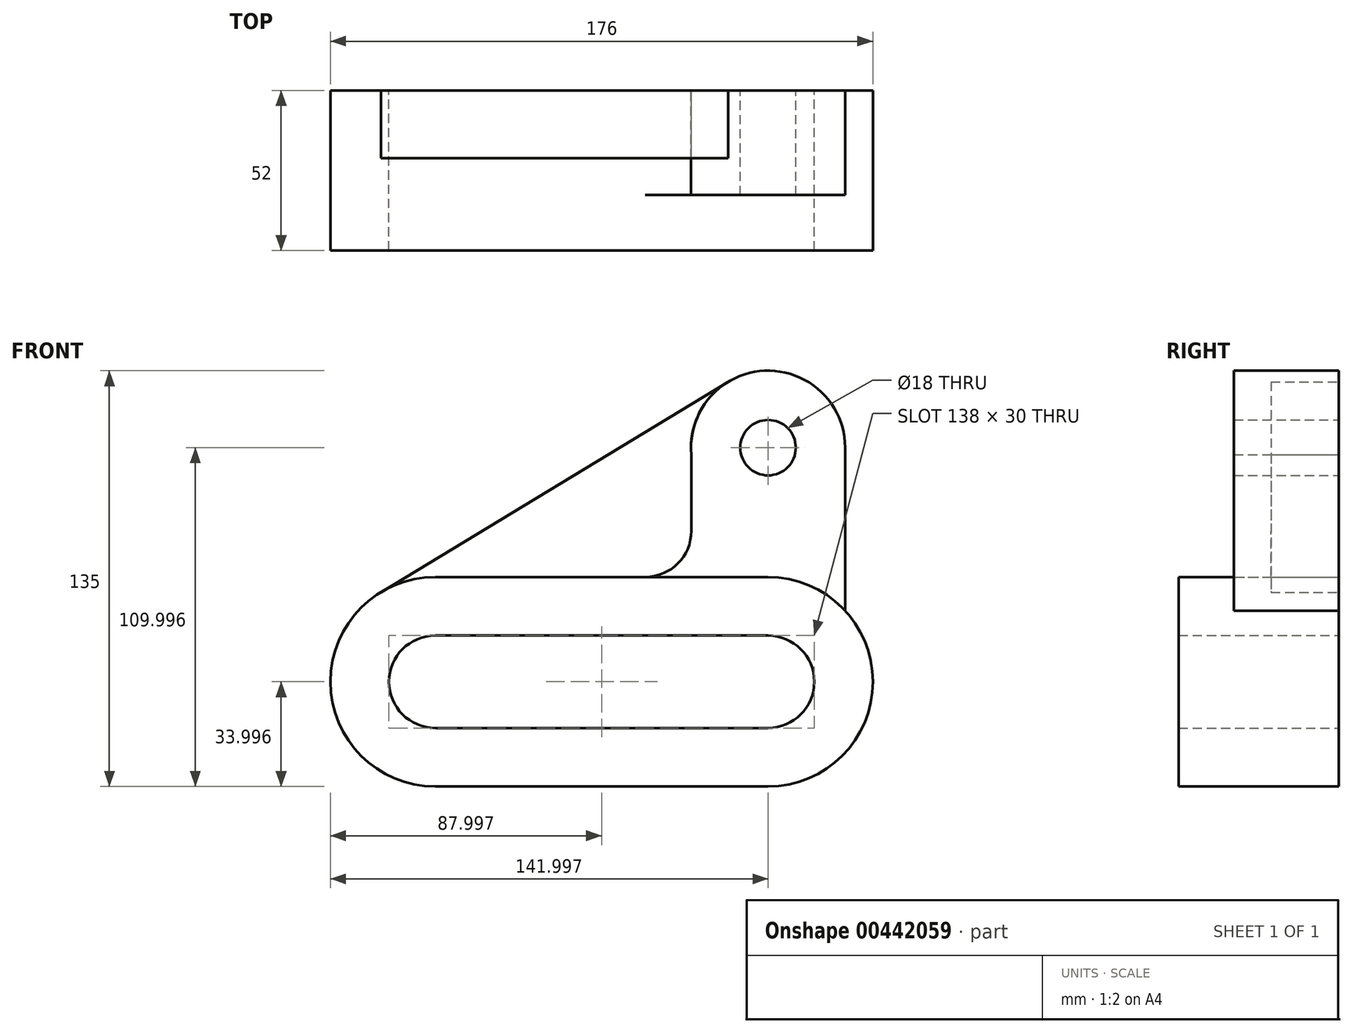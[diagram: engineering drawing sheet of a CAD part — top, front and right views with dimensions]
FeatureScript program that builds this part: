
annotation { "Feature Type Name" : "Feature", "Feature Type Description" : "" }
export const myFeature = defineFeature(function(context is Context, id is Id, definition is map)
    precondition{}
    {
        {
            var Q0;
            Q0=qCreatedBy(makeId("Front.planeOp"),FACE);
            var sketch = newSketch(context, id + "F0", { "sketchPlane" : qUnion([Q0])});
            skCircle(sketch, "E0", {"center": v(33.69, 22.6) * mm, "radius": 9 * mm});
            skCircle(sketch, "E1", {"center": v(33.69, 22.6) * mm, "radius": 25 * mm});
            skLineSegment(sketch, "E2.bottom", {"start": v(-74.31, -19.4) * mm, "end": v(-6.21, -19.4) * mm});
            skLineSegment(sketch, "E2.top", {"start": v(-74.31, -87.4) * mm, "end": v(33.69, -87.4) * mm});
            skLineSegment(sketch, "E2.left", {"start": v(-74.31, -19.4) * mm, "end": v(-74.31, -87.4) * mm});
            skLineSegment(sketch, "E2.right", {"start": v(33.69, -19.4) * mm, "end": v(33.69, -87.4) * mm});
            skCircle(sketch, "E3", {"center": v(-74.31, -53.4) * mm, "radius": 34 * mm});
            skCircle(sketch, "E4", {"center": v(33.69, -53.4) * mm, "radius": 34 * mm});
            skArc(sketch, "E5", {"start": v(-74.31, -38.4) * mm, "mid": v(-89.31, -53.4) * mm, "end": v(-74.31, -68.4) * mm});
            skArc(sketch, "E6", {"start": v(33.69, -68.4) * mm, "mid": v(48.69, -53.4) * mm, "end": v(33.69, -38.4) * mm});
            skLineSegment(sketch, "E7", {"start": v(-74.31, -38.4) * mm, "end": v(33.69, -38.4) * mm});
            skLineSegment(sketch, "E8", {"start": v(-74.31, -68.4) * mm, "end": v(33.69, -68.4) * mm});
            skLineSegment(sketch, "E9", {"start": v(20.73, 43.98) * mm, "end": v(-91.94, -24.32) * mm});
            skLineSegment(sketch, "E10", {"start": v(92.33, 22.6) * mm, "end": v(-33.36, 22.6) * mm});
            skLineSegment(sketch, "E11", {"start": v(58.69, 22.6) * mm, "end": v(58.69, -30.35) * mm});
            skLineSegment(sketch, "E12", {"start": v(8.79, 20.34) * mm, "end": v(8.79, -4.4) * mm});
            skArc(sketch, "E13.filletArc", {"start": v(-6.21, -19.4) * mm, "mid": v(4.4, -15) * mm, "end": v(8.79, -4.4) * mm});
            skLineSegment(sketch, "E14", {"start": v(-6.21, -19.4) * mm, "end": v(33.69, -19.4) * mm});
            skSolve(sketch);
        }
        {
            var Q0;
            {var subQ6=sQuery(id+"F0.wireOp",EDGE,"E2.bottom");Q0=makeQuery(id+"F0.imprint","IMPRINT",FACE,{"disambiguationData":[TD([[makeQuery(id+"F0.imprint","IMPRINT",EDGE,{"derivedFrom":subQ6}),-1.0]])]});}
            var Q1;
            {var subQ0=sQuery(id+"F0.wireOp",EDGE,"E3");var subQ3=sQuery(id+"F0.wireOp",EDGE,"E7");var subQ5=makeQuery(id+"F0.imprint","INTERSECT",VERTEX,{"derivedFrom":[subQ0,subQ3]});Q1=makeQuery(id+"F0.imprint","IMPRINT",FACE,{"disambiguationData":[TD([[makeQuery(id+"F0.imprint","IMPRINT",EDGE,{"disambiguationData":[TD([[subQ5,-1.0]])],"derivedFrom":subQ0}),1.0]])]});}
            var Q2;
            {var subQ5=sQuery(id+"F0.wireOp",EDGE,"E5");Q2=makeQuery(id+"F0.imprint","IMPRINT",FACE,{"disambiguationData":[TD([[makeQuery(id+"F0.imprint","IMPRINT",EDGE,{"derivedFrom":subQ5}),-1.0]])]});}
            var Q3;
            {var subQ0=sQuery(id+"F0.wireOp",EDGE,"E3");var subQ3=sQuery(id+"F0.wireOp",EDGE,"E8");var subQ5=makeQuery(id+"F0.imprint","INTERSECT",VERTEX,{"derivedFrom":[subQ0,subQ3]});Q3=makeQuery(id+"F0.imprint","IMPRINT",FACE,{"disambiguationData":[TD([[makeQuery(id+"F0.imprint","IMPRINT",EDGE,{"disambiguationData":[TD([[subQ5,1.0]])],"derivedFrom":subQ0}),1.0]])]});}
            var Q4;
            {var subQ0=sQuery(id+"F0.wireOp",EDGE,"E2.top");Q4=makeQuery(id+"F0.imprint","IMPRINT",FACE,{"disambiguationData":[TD([[makeQuery(id+"F0.imprint","IMPRINT",EDGE,{"derivedFrom":subQ0}),1.0]])]});}
            var Q5;
            {var subQ0=sQuery(id+"F0.wireOp",EDGE,"E4");var subQ3=sQuery(id+"F0.wireOp",EDGE,"E8");var subQ5=makeQuery(id+"F0.imprint","INTERSECT",VERTEX,{"derivedFrom":[subQ0,subQ3]});Q5=makeQuery(id+"F0.imprint","IMPRINT",FACE,{"disambiguationData":[TD([[makeQuery(id+"F0.imprint","IMPRINT",EDGE,{"disambiguationData":[TD([[subQ5,-1.0]])],"derivedFrom":subQ0}),1.0]])]});}
            var Q6;
            {var subQ5=sQuery(id+"F0.wireOp",EDGE,"E6");Q6=makeQuery(id+"F0.imprint","IMPRINT",FACE,{"disambiguationData":[TD([[makeQuery(id+"F0.imprint","IMPRINT",EDGE,{"derivedFrom":subQ5}),-1.0]])]});}
            var Q7;
            {var subQ0=sQuery(id+"F0.wireOp",EDGE,"E4");var subQ3=sQuery(id+"F0.wireOp",EDGE,"E7");var subQ5=makeQuery(id+"F0.imprint","INTERSECT",VERTEX,{"derivedFrom":[subQ0,subQ3]});Q7=makeQuery(id+"F0.imprint","IMPRINT",FACE,{"disambiguationData":[TD([[makeQuery(id+"F0.imprint","IMPRINT",EDGE,{"disambiguationData":[TD([[subQ5,1.0]])],"derivedFrom":subQ0}),1.0]])]});}
            extrude(context, id + "F1", {"entities" : qUnion([Q0, Q1, Q2, Q3, Q4, Q5, Q6, Q7]), "depth" : 52 * mm});
        }
        {
            var Q0;
            {var subQ0=sQuery(id+"F0.wireOp",EDGE,"E10");var subQ4=sQuery(id+"F0.wireOp",EDGE,"E0");var subQ5=makeQuery(id+"F0.imprint","INTERSECT",VERTEX,{"disambiguationData":[OD(0.0)],"derivedFrom":[subQ4,subQ0]});Q0=makeQuery(id+"F0.imprint","IMPRINT",FACE,{"disambiguationData":[TD([[makeQuery(id+"F0.imprint","IMPRINT",EDGE,{"disambiguationData":[TD([[subQ5,1.0]])],"derivedFrom":subQ4}),-1.0]])]});}
            var Q1;
            {var subQ0=sQuery(id+"F0.wireOp",EDGE,"E10");var subQ3=sQuery(id+"F0.wireOp",EDGE,"E0");var subQ4=makeQuery(id+"F0.imprint","INTERSECT",VERTEX,{"disambiguationData":[OD(0.0)],"derivedFrom":[subQ3,subQ0]});Q1=makeQuery(id+"F0.imprint","IMPRINT",FACE,{"disambiguationData":[TD([[makeQuery(id+"F0.imprint","IMPRINT",EDGE,{"disambiguationData":[TD([[subQ4,-1.0]])],"derivedFrom":subQ3}),-1.0]])]});}
            var Q2;
            {var subQ0=sQuery(id+"F0.wireOp",EDGE,"E11");Q2=makeQuery(id+"F0.imprint","IMPRINT",FACE,{"disambiguationData":[TD([[makeQuery(id+"F0.imprint","IMPRINT",EDGE,{"derivedFrom":subQ0}),-1.0]])]});}
            extrude(context, id + "F2", {"entities" : qUnion([Q0, Q1, Q2]), "operationType" : NewBodyOperationType.ADD, "depth" : 34 * mm});
        }
        {
            var Q0;
            {var subQ5=sQuery(id+"F0.wireOp",EDGE,"E2.bottom");Q0=makeQuery(id+"F0.imprint","IMPRINT",FACE,{"disambiguationData":[TD([[makeQuery(id+"F0.imprint","IMPRINT",EDGE,{"derivedFrom":subQ5}),1.0]])]});}
            var Q1;
            {var subQ0=sQuery(id+"F0.wireOp",EDGE,"E9");var subQ1=sQuery(id+"F0.wireOp",EDGE,"E1");var subQ2=makeQuery(id+"F0.imprint","INTERSECT",VERTEX,{"derivedFrom":[subQ1,subQ0]});Q1=makeQuery(id+"F0.imprint","IMPRINT",FACE,{"disambiguationData":[TD([[makeQuery(id+"F0.imprint","IMPRINT",EDGE,{"disambiguationData":[TD([[subQ2,-1.0]])],"derivedFrom":subQ1}),-1.0]])]});}
            var Q2;
            Q2=sQuery(id+"F0.wireOp",EDGE,"E9");
            extrude(context, id + "F3", {"entities" : qUnion([Q0, Q1]), "surfaceEntities" : qUnion([Q2]), "depth" : 22 * mm});
        }
    });
